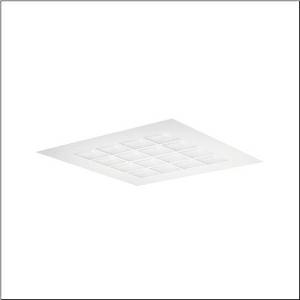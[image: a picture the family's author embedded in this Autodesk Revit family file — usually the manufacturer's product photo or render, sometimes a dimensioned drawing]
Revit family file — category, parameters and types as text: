
# Revit family: scriptus_r__11_5mz312ledzm00191xx_ec59
name_source: partatom
category: Lighting Fixtures
units: mm (PartAtom-declared; Revit-internal decimal feet)

## family parameters
Cut with Voids When Loaded = No
Host = Face
Light Source = No
Part Type = Normal
Room Calculation Point = No
Round Connector Dimension = Use Diameter
Shared = No

## types (1)
- --- (1 x LED, 6400 lm, 43 W, 4000K)
    Apparent Load = 43 VA
    CIE Flux Codes = 80 95 99 100 100
    Color Rendering = 80
    Color Temperature = 4000K
    Default Elevation = 1800 mm
    Description = Scriptus® 11, office luminaire, primary optical cover: lenses, CAT 2 (L<= 3000cd/m²), light emission: direct distribution, primary light characteristic: symmetric, installation type: lay-in mounting, LED, rated luminous flux: 6.400lm, light colour: 840, colour temperature: 4000K, control gear: ECG DALI, with terminal, 3+2-pole, max. 2.5mm², mains connection: 230V, AC, 50Hz, housing, of sheet steel, galvanised, traffic white (RAL 9016), module: M625, length: 621mm, width: 621mm, height: 68mm, protection rating (complete): IP20, insulation class (complete): insulation class I (protective earthing), certification: CE, impact resistance: IK02, permissible operating ambient temperature: 0..+35°C, standard: EN 50419, packaging unit: 1 piece
    Height = 80 mm  [stored 0.262467 ft]
    Lamp = 1 x LED
    Lamp Light Flux = 6400 lm
    Lamp Power = 43 W
    Lamp count = 1
    Length = 622 mm
    Luminous efficacy = 149 lm/W
    Manufacturer = Siteco
    ModVariant = No
    Model = 5MZ312LEDZM00191XX
    Mounting Place = Ceiling
    Mounting Type = Pendant
    Number of Poles = 1
    OnlyDefault = Yes
    Power Factor = 1
    Product Name = Scriptus® 11
    Product group = office luminaire | ceiling pendant
    ProductGroupID = 905
    Protection Class = Protection class I
    Protection Degree = IP 20
    RLX_Detail_Level = 1
    RlxData = <blob elided: 22833 chars, md5=b2ee2270>
    Socket = socket
    Standby Power = 0 W
    System Light Flux = 6400 lm
    System Power = 43 W
    Type Comments = factory setting: luminous flux: 100 % | dim-lin: 254 | 227 mA
    Type Image = l_1006857.jpg
    URL = http://relux.com
    VarID = @adj_117543
    Voltage = 0 V
    Weight = 0.00 kg
    Width = 622 mm

note: [stored X ft] marks values corroborated as IEEE doubles in the binary element streams (Revit-internal decimal feet)

## geometry (parser evidence)
native form markers: Blend x4, Sweep x10
no freeform markers — native parametric forms only
